# Revit family: Water-Closet_Carrier-Josam-12674
name_source: partatom
category: Plumbing Fixtures
revit_build: Autodesk Revit MEP 2012 (Build: 20110309_2315(x64)
units: mm (PartAtom-declared; Revit-internal decimal feet)

## types (1)
- Left Hand
    04 CSI = 22 40 00
    Default Elevation = 48"
    Description = 12674 Water Closet Carrier
    Fixture Offset = 4 1/2"
    Inner Pipe Radius = 2 7/32"
    Manufacturer = Josam Company
    Manufacturer Fax = 800-627-0008
    Model = 12674
    Outer Pipe Radius = 2 29/64"
    Pipe Diameter = 3 29/32"
    Pipe Outer Dia = 4 29/64"
    Pipe Radius = 1 61/64"
    Product Line = Josam
    Product Page URL = http://www.josam.com
    Product Type = Single
    Stud = Metal - Josam - Brass - Satin
    Stud Lenght = 5 5/64"
    Subcategory = Closet Carrier
    URL = http://www.josam.com
    Unit = Metal - Josam - Anodized- Dark Bronze Satin

## geometry (parser evidence)
native form markers: Sweep x10
no freeform markers — native parametric forms only
